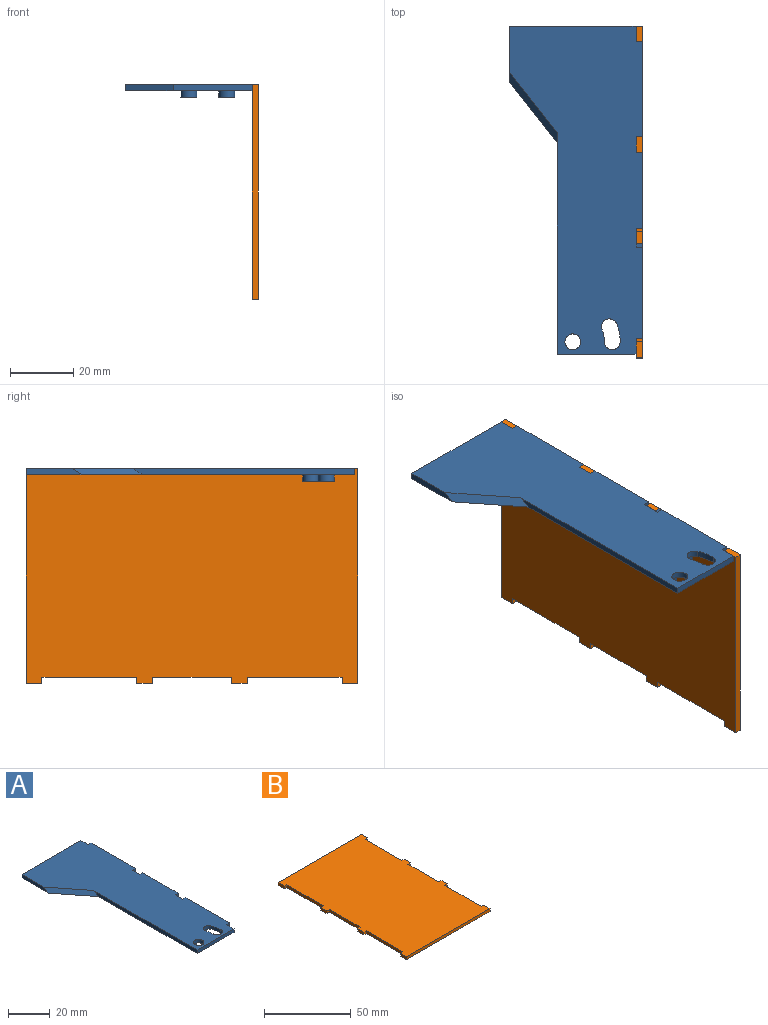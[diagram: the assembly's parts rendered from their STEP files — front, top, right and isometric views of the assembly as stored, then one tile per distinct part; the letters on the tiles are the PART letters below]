
ASSEMBLY  parts=2 mates=1
PART A: 29 faces, bbox 42x104x4 mm
  f0: plane 40x2mm, normal (0,1,0), area 80mm2, adj f1,f2,f8,f28
  f1: plane 104x42mm, normal (0,0,1), area 3068.3mm2, adj f0,f3,f4,f5,f6,f7,f8,f13
  f2: plane 104x42mm, normal (0,0,-1), area 3077.4mm2, adj f0,f3,f4,f5,f6,f7,f8,f9
  f3: plane 30x2mm, normal (1,0,0), area 60mm2, adj f1,f2,f24,f27
  f4: plane 30x2mm, normal (1,0,0), area 60mm2, adj f1,f2,f20,f22
  f5: plane 70.23x2mm, normal (-1,0,0), area 137.2mm2, adj f1,f2,f6,f18
  f6: plane 25x2mm, normal (0,-1,0), area 50mm2, adj f1,f2,f5,f23
  f7: plane 24x2mm, normal (1,0,0), area 48mm2, adj f1,f2,f21,f26
  f8: plane 18x2mm, normal (-1,0,0), area 32.8mm2, adj f0,f1,f2,f18
  f9: cylinder r=2.5mm len=5mm, axis (0,0,1), area 31.4mm2, adj f2,f10
  f10: plane 5x5mm, normal (0,0,-1), area 19.6mm2, adj f9
  f11: cylinder r=2.5mm len=5mm, axis (0,0,1), area 31.4mm2, adj f2,f12
  f12: plane 5x5mm, normal (0,0,-1), area 19.6mm2, adj f11
  f13: cylinder r=10mm len=3.83mm, axis (0,0,-1), area 7.9mm2, adj f1,f2,f14,f16
  f14: cylinder r=2.5mm len=5mm, axis (0,0,-1), area 15.7mm2, adj f1,f2,f13,f15
  f15: cylinder r=15mm len=5.74mm, axis (0,0,-1), area 11.8mm2, adj f1,f2,f14,f16
  f16: cylinder r=2.5mm len=4.81mm, axis (0,0,-1), area 15.7mm2, adj f1,f2,f13,f15
  f17: cylinder r=2.5mm len=5mm, axis (0,0,-1), area 31.4mm2, adj f1,f2
  f18: plane 22.23x15mm, normal (-0.55,-0.44,0.71), area 68.5mm2, adj f1,f2,f5,f8
  f19: plane 5x2mm, normal (1,0,0), area 10mm2, adj f1,f2,f20,f21
  f20: plane 2x2mm, normal (0,1,0), area 4mm2, adj f1,f2,f4,f19
  f21: plane 2x2mm, normal (0,-1,0), area 4mm2, adj f1,f2,f7,f19
  f22: plane 2x2mm, normal (0,-1,0), area 4mm2, adj f1,f2,f4,f23
  f23: plane 5x2mm, normal (1,0,0), area 10mm2, adj f1,f2,f6,f22
  f24: plane 2x2mm, normal (0,-1,0), area 4mm2, adj f1,f2,f3,f25
  f25: plane 5x2mm, normal (1,0,0), area 10mm2, adj f1,f2,f24,f26
  f26: plane 2x2mm, normal (0,1,0), area 4mm2, adj f1,f2,f7,f25
  f27: plane 2x2mm, normal (0,1,0), area 4mm2, adj f1,f2,f3,f28
  f28: plane 5x2mm, normal (1,0,0), area 10mm2, adj f0,f1,f2,f27
PART B: 30 faces, bbox 68x105x2 mm
  f0: plane 2x2mm, normal (0,1,0), area 4mm2, adj f1,f27,f28,f29
  f1: plane 25x2mm, normal (1,0,0), area 50mm2, adj f0,f2,f28,f29
  f2: plane 2x2mm, normal (0,-1,0), area 4mm2, adj f1,f3,f28,f29
  f3: plane 5x2mm, normal (1,0,0), area 10mm2, adj f2,f4,f28,f29
  f4: plane 2x2mm, normal (0,1,0), area 4mm2, adj f3,f5,f28,f29
  f5: plane 30x2mm, normal (1,0,0), area 60mm2, adj f4,f6,f28,f29
  f6: plane 2x2mm, normal (0,-1,0), area 4mm2, adj f5,f7,f28,f29
  f7: plane 5x2mm, normal (1,0,0), area 10mm2, adj f6,f8,f28,f29
  f8: plane 68x2mm, normal (0,1,0), area 136mm2, adj f7,f9,f28,f29
  f9: plane 5x2mm, normal (-1,0,0), area 10mm2, adj f8,f10,f28,f29
  f10: plane 2x2mm, normal (0,-1,0), area 4mm2, adj f9,f11,f28,f29
  f11: plane 30x2mm, normal (-1,0,0), area 60mm2, adj f10,f12,f28,f29
  f12: plane 2x2mm, normal (0,1,0), area 4mm2, adj f11,f13,f28,f29
  f13: plane 5x2mm, normal (-1,0,0), area 10mm2, adj f12,f14,f28,f29
  f14: plane 2x2mm, normal (0,-1,0), area 4mm2, adj f13,f15,f28,f29
  f15: plane 25x2mm, normal (-1,0,0), area 50mm2, adj f14,f16,f28,f29
  f16: plane 2x2mm, normal (0,1,0), area 4mm2, adj f15,f17,f28,f29
  f17: plane 5x2mm, normal (-1,0,0), area 10mm2, adj f16,f18,f28,f29
  f18: plane 2x2mm, normal (0,-1,0), area 4mm2, adj f17,f19,f28,f29
  f19: plane 30x2mm, normal (-1,0,0), area 60mm2, adj f18,f20,f28,f29
  f20: plane 2x2mm, normal (0,1,0), area 4mm2, adj f19,f21,f28,f29
  f21: plane 5x2mm, normal (-1,0,0), area 10mm2, adj f20,f22,f28,f29
  f22: plane 68x2mm, normal (0,-1,0), area 136mm2, adj f21,f23,f28,f29
  f23: plane 5x2mm, normal (1,0,0), area 10mm2, adj f22,f24,f28,f29
  f24: plane 2x2mm, normal (0,1,0), area 4mm2, adj f23,f25,f28,f29
  f25: plane 30x2mm, normal (1,0,0), area 60mm2, adj f24,f26,f28,f29
  f26: plane 2x2mm, normal (0,-1,0), area 4mm2, adj f25,f27,f28,f29
  f27: plane 5x2mm, normal (1,0,0), area 10mm2, adj f0,f26,f28,f29
  f28: plane 105x68mm, normal (0,0,1), area 6800mm2, adj f0,f1,f2,f3,f4,f5,f6,f7
  f29: plane 105x68mm, normal (0,0,-1), area 6800mm2, adj f0,f1,f2,f3,f4,f5,f6,f7
PLACE A t=(-5.67,-49.53,0)mm
PLACE B rot(axis=(0,1,0),90deg) t=(14.33,-8.74,-35.18)mm
MATE fastened B.f29 <-> A.f28  axis (-1,0,0) through (14.33,42.97,2)mm
